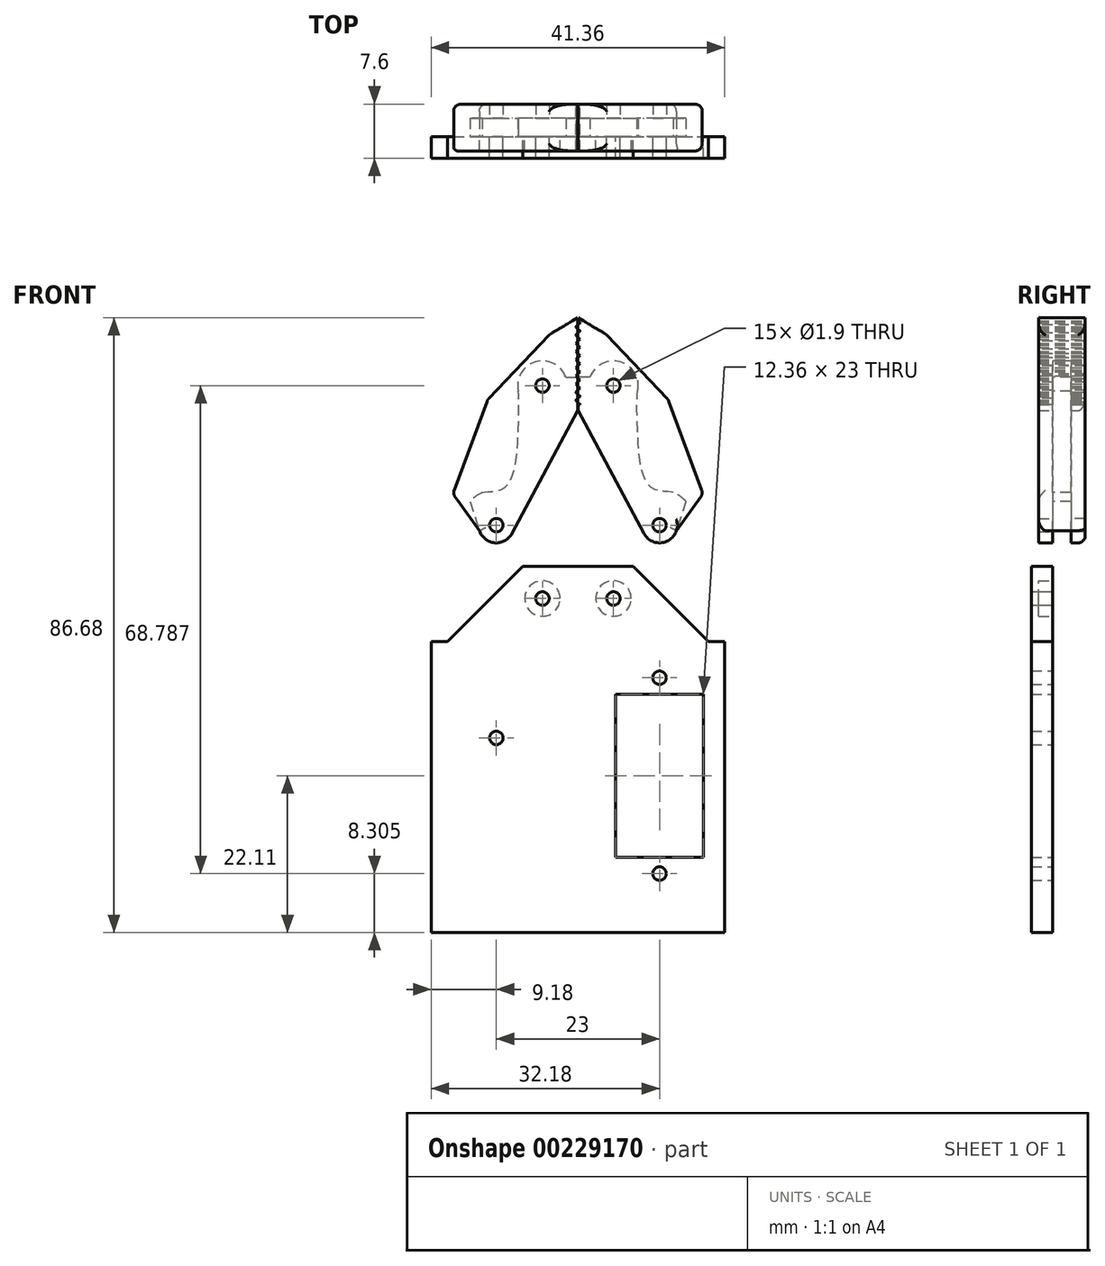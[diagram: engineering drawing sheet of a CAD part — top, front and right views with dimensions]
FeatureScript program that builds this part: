
annotation { "Feature Type Name" : "Feature", "Feature Type Description" : "" }
export const myFeature = defineFeature(function(context is Context, id is Id, definition is map)
    precondition{}
    {
        {
            var Q0;
            Q0=qCreatedBy(makeId("Front.planeOp"),FACE);
            var sketch = newSketch(context, id + "F0", { "sketchPlane" : qUnion([Q0])});
            skLineSegment(sketch, "E0.top", {"start": v(17.68, -22.43) * mm, "end": v(5.32, -22.43) * mm});
            skLineSegment(sketch, "E0.left", {"start": v(18.36, 12.56) * mm, "end": v(18.36, -22.43) * mm});
            skLineSegment(sketch, "E0.right", {"start": v(-18.36, 12.56) * mm, "end": v(-18.36, -22.43) * mm});
            skPoint(sketch, "E0.middle", {"position": v(0, 0) * mm});
            skLineSegment(sketch, "E1.bottom", {"start": v(5.32, -22.43) * mm, "end": v(17.68, -22.43) * mm});
            skLineSegment(sketch, "E1.top", {"start": v(5.32, 5.18) * mm, "end": v(17.68, 5.18) * mm});
            skLineSegment(sketch, "E1.left", {"start": v(5.32, -22.43) * mm, "end": v(5.32, 5.18) * mm});
            skLineSegment(sketch, "E1.right", {"start": v(17.68, -22.43) * mm, "end": v(17.68, 5.18) * mm});
            skLineSegment(sketch, "E2.bottom", {"start": v(5.32, 0) * mm, "end": v(17.68, 0) * mm});
            skLineSegment(sketch, "E2.top", {"start": v(5.32, -17.82) * mm, "end": v(17.68, -17.82) * mm});
            skLineSegment(sketch, "E2.left", {"start": v(5.32, 0) * mm, "end": v(5.32, -17.82) * mm});
            skLineSegment(sketch, "E2.right", {"start": v(17.68, 0) * mm, "end": v(17.68, -17.82) * mm});
            skLineSegment(sketch, "E3.bottom", {"start": v(17.68, 5.18) * mm, "end": v(5.32, 5.18) * mm});
            skLineSegment(sketch, "E3.top", {"start": v(17.68, 9.8) * mm, "end": v(5.32, 9.8) * mm});
            skLineSegment(sketch, "E3.left", {"start": v(17.68, 5.18) * mm, "end": v(17.68, 9.8) * mm});
            skLineSegment(sketch, "E3.right", {"start": v(5.32, 5.18) * mm, "end": v(5.32, 9.8) * mm});
            skLineSegment(sketch, "E4", {"start": v(5.32, 9.8) * mm, "end": v(17.68, 5.18) * mm, "construction": true});
            skLineSegment(sketch, "E5", {"start": v(5.32, -17.82) * mm, "end": v(17.68, -22.43) * mm, "construction": true});
            skCircle(sketch, "E6", {"center": v(11.5, 7.49) * mm, "radius": 0.95 * mm});
            skLineSegment(sketch, "E7.top", {"start": v(-18.36, -25.43) * mm, "end": v(18.36, -25.43) * mm});
            skLineSegment(sketch, "E7.left", {"start": v(-18.36, -22.43) * mm, "end": v(-18.36, -25.43) * mm});
            skLineSegment(sketch, "E7.right", {"start": v(18.36, -22.43) * mm, "end": v(18.36, -25.43) * mm});
            skLineSegment(sketch, "E8", {"start": v(0, 32.14) * mm, "end": v(0, 0) * mm, "construction": true});
            skLineSegment(sketch, "E9", {"start": v(-18.36, 0) * mm, "end": v(18.36, 0) * mm, "construction": true});
            skCircle(sketch, "E10", {"center": v(11.5, -20.12) * mm, "radius": 0.95 * mm});
            skLineSegment(sketch, "E11.top", {"start": v(-18.36, -28.43) * mm, "end": v(18.36, -28.43) * mm});
            skLineSegment(sketch, "E11.left", {"start": v(-18.36, -25.43) * mm, "end": v(-18.36, -28.43) * mm});
            skLineSegment(sketch, "E11.right", {"start": v(18.36, -25.43) * mm, "end": v(18.36, -28.43) * mm});
            skLineSegment(sketch, "E12", {"start": v(-18.36, 12.56) * mm, "end": v(-7.75, 23.16) * mm});
            skLineSegment(sketch, "E13", {"start": v(7.75, 23.16) * mm, "end": v(18.36, 12.56) * mm});
            skLineSegment(sketch, "E14", {"start": v(-18.36, 12.56) * mm, "end": v(-18.36, 23.16) * mm, "construction": true});
            skLineSegment(sketch, "E15", {"start": v(18.36, 12.56) * mm, "end": v(18.36, 23.49) * mm, "construction": true});
            skCircle(sketch, "E16", {"center": v(-5, 18.66) * mm, "radius": 0.95 * mm});
            skCircle(sketch, "E17", {"center": v(5, 18.66) * mm, "radius": 0.95 * mm});
            skCircle(sketch, "E18", {"center": v(-11.5, -1) * mm, "radius": 0.95 * mm});
            skLineSegment(sketch, "E19", {"start": v(-7.75, 23.16) * mm, "end": v(7.75, 23.16) * mm});
            skCircle(sketch, "E20", {"center": v(11.5, -1) * mm, "radius": 6.18 * mm});
            skLineSegment(sketch, "E21", {"start": v(11.5, -1) * mm, "end": v(-6.79, -1) * mm, "construction": true});
            skLineSegment(sketch, "E22", {"start": v(-10.25, -1) * mm, "end": v(-10.25, 21.43) * mm, "construction": true});
            skLineSegment(sketch, "E23", {"start": v(18.36, 12.56) * mm, "end": v(20.68, 12.56) * mm});
            skLineSegment(sketch, "E24", {"start": v(20.68, 12.56) * mm, "end": v(20.68, -28.43) * mm});
            skLineSegment(sketch, "E25", {"start": v(-18.36, 12.56) * mm, "end": v(-20.68, 12.56) * mm});
            skLineSegment(sketch, "E26", {"start": v(-20.68, 12.56) * mm, "end": v(-20.68, -28.43) * mm});
            skLineSegment(sketch, "E27", {"start": v(-20.68, -28.43) * mm, "end": v(-18.36, -28.43) * mm});
            skLineSegment(sketch, "E28", {"start": v(18.36, -25.43) * mm, "end": v(20.68, -25.43) * mm});
            skLineSegment(sketch, "E29", {"start": v(20.68, -25.43) * mm, "end": v(-20.68, -25.43) * mm});
            skLineSegment(sketch, "E30", {"start": v(20.68, -28.43) * mm, "end": v(18.36, -28.43) * mm});
            skSolve(sketch);
        }
        {
            var Q0;
            {var subQ1=makeQuery(id+"F0.imprint","IMPRINT",EDGE,{"derivedFrom":sQuery(id+"F0.wireOp",EDGE,"E7.top")});var subQ9=makeQuery(id+"F0.imprint","IMPRINT",EDGE,{"derivedFrom":sQuery(id+"F0.wireOp",EDGE,"E0.right")});var subQ10=makeQuery(id+"F0.imprint","IMPRINT",EDGE,{"derivedFrom":sQuery(id+"F0.wireOp",EDGE,"E0.left")});var subQ16=sQuery(id+"F0.wireOp",EDGE,"E0.top");var subQ20=makeQuery(id+"F0.imprint","IMPRINT",EDGE,{"derivedFrom":sQuery(id+"F0.wireOp",EDGE,"E11.left")});var subQ21=makeQuery(id+"F0.imprint","IMPRINT",EDGE,{"derivedFrom":sQuery(id+"F0.wireOp",EDGE,"E11.right")});Q0=qUnion([makeQuery(id+"F0.imprint","IMPRINT",FACE,{"disambiguationData":[TD([[subQ10,1.0]])]}),makeQuery(id+"F0.imprint","IMPRINT",FACE,{"disambiguationData":[TD([[subQ9,-1.0]])]}),makeQuery(id+"F0.imprint","IMPRINT",FACE,{"disambiguationData":[TD([[subQ20,-1.0]])]}),makeQuery(id+"F0.imprint","IMPRINT",FACE,{"disambiguationData":[TD([[subQ21,1.0]])]}),makeQuery(id+"F0.imprint","IMPRINT",FACE,{"disambiguationData":[TD([[subQ1,-1.0]])]}),makeQuery(id+"F0.imprint","IMPRINT",FACE,{"disambiguationData":[TD([[makeQuery(id+"F0.imprint","IMPRINT",EDGE,{"derivedFrom":subQ16}),1.0]])]})]);}
            var Q1;
            {var subQ2=sQuery(id+"F0.wireOp",EDGE,"E0.top");Q1=makeQuery(id+"F0.imprint","IMPRINT",FACE,{"disambiguationData":[TD([[makeQuery(id+"F0.imprint","IMPRINT",EDGE,{"derivedFrom":subQ2}),-1.0]])]});}
            var Q2;
            Q2=makeQuery(id+"F0.imprint","IMPRINT",FACE,{"disambiguationData":[TD([[makeQuery(id+"F0.imprint","IMPRINT",EDGE,{"derivedFrom":sQuery(id+"F0.wireOp",EDGE,"E3.top")}),1.0]])]});
            var Q3;
            {var subQ0=sQuery(id+"F0.wireOp",EDGE,"E3.bottom");var subQ1=sQuery(id+"F0.wireOp",EDGE,"FkeFUImi-7huS-bPcJ-8ver-gJrOx2cKMFpE");var subQ2=makeQuery(id+"F0.imprint","INTERSECT",VERTEX,{"disambiguationData":[OD(0.0)],"derivedFrom":[subQ1,subQ0]});Q3=makeQuery(id+"F0.imprint","IMPRINT",FACE,{"disambiguationData":[TD([[makeQuery(id+"F0.imprint","IMPRINT",EDGE,{"disambiguationData":[TD([[subQ2,-1.0]])],"derivedFrom":subQ1}),1.0]])]});}
            extrude(context, id + "F1", {"entities" : qUnion([Q0, Q1, Q2, Q3]), "depth" : 3 * mm});
        }
        {
            var Q0;
            Q0=makeQuery(id+"F0.imprint","IMPRINT",FACE,{"disambiguationData":[TD([[makeQuery(id+"F0.imprint","IMPRINT",EDGE,{"derivedFrom":sQuery(id+"F0.wireOp",EDGE,"E0.left")}),-1.0]])]});
            var sketch = newSketch(context, id + "F2", { "sketchPlane" : qUnion([Q0])});
            skCircle(sketch, "E31", {"center": v(-5, 18.66) * mm, "radius": 0.95 * mm});
            skCircle(sketch, "E32", {"center": v(5, 18.66) * mm, "radius": 0.95 * mm});
            skCircle(sketch, "E33", {"center": v(5, 18.66) * mm, "radius": 2.5 * mm});
            skCircle(sketch, "E34", {"center": v(-5, 18.66) * mm, "radius": 2.5 * mm});
            skCircle(sketch, "E35", {"center": v(-5, 48.66) * mm, "radius": 2.5 * mm});
            skLineSegment(sketch, "E36", {"start": v(-5, 18.66) * mm, "end": v(-5, 48.66) * mm});
            skLineSegment(sketch, "E37", {"start": v(-11.5, -1) * mm, "end": v(-11.5, 29) * mm});
            skCircle(sketch, "E38", {"center": v(-11.5, 29) * mm, "radius": 2.5 * mm});
            skCircle(sketch, "E39", {"center": v(-5, 48.66) * mm, "radius": 0.95 * mm});
            skCircle(sketch, "E40", {"center": v(-11.5, 29) * mm, "radius": 0.95 * mm});
            skLineSegment(sketch, "E41", {"start": v(0, 85.35) * mm, "end": v(-3, 85.35) * mm});
            skLineSegment(sketch, "E42", {"start": v(-21.12, 18.52) * mm, "end": v(-21.12, 50.54) * mm, "construction": true});
            skLineSegment(sketch, "E43.direction1", {"start": v(0, 82.52) * mm, "end": v(25, 82.52) * mm, "construction": true});
            skLineSegment(sketch, "E43.direction2", {"start": v(0, 82.52) * mm, "end": v(0, 82.52) * mm, "construction": true});
            skLineSegment(sketch, "E44.trimOffspring", {"start": v(-0.3, 51.2) * mm, "end": v(-0.3, 51.2) * mm});
            skLineSegment(sketch, "E45.trimOffspring", {"start": v(0, 82.52) * mm, "end": v(0, 82.52) * mm});
            skLineSegment(sketch, "E46", {"start": v(0, 45.16) * mm, "end": v(-9.3, 27.82) * mm});
            skLineSegment(sketch, "E47", {"start": v(-15.21, 32.35) * mm, "end": v(-13.88, 28.23) * mm});
            skArc(sketch, "E48", {"start": v(-13.46, 33.6) * mm, "mid": v(-14.4, 33.07) * mm, "end": v(-15.21, 32.35) * mm});
            skLineSegment(sketch, "E49", {"start": v(0, 85.35) * mm, "end": v(0, 73.2) * mm});
            skLineSegment(sketch, "E50.trimOffspring", {"start": v(0, 54.96) * mm, "end": v(0, 45.16) * mm});
            skPoint(sketch, "E51.visualSharp", {"position": v(-12.13, 33.96) * mm});
            skLineSegment(sketch, "E52", {"start": v(0, 54.96) * mm, "end": v(0, 73.2) * mm});
            skLineSegment(sketch, "E53", {"start": v(-3.95, 55.9) * mm, "end": v(0, 58.26) * mm});
            skLineSegment(sketch, "E54", {"start": v(0, 58.26) * mm, "end": v(-3.95, 55.9) * mm});
            skLineSegment(sketch, "E55", {"start": v(-2.5, 48.79) * mm, "end": v(-2.5, 18.66) * mm, "construction": true});
            skLineSegment(sketch, "E56", {"start": v(-7.5, 48.66) * mm, "end": v(-7.5, 18.66) * mm, "construction": true});
            skFitSpline(sketch, "E57", {"points": [v(-13.46, 33.6) * mm, v(-10.5, 34.2) * mm, v(-8.48, 40.92) * mm, v(-8.42, 47.9) * mm], "startDerivative": vector(5.15, 2.53) * mm, "endDerivative": vector(-1.23, 9.61) * mm});
            skCircle(sketch, "E58", {"center": v(-5, 48.66) * mm, "radius": 3.5 * mm});
            skLineSegment(sketch, "E59", {"start": v(-3.95, 55.9) * mm, "end": v(-6.13, 53.44) * mm});
            skLineSegment(sketch, "E60", {"start": v(-12.74, 46.65) * mm, "end": v(-17.64, 33.43) * mm});
            skLineSegment(sketch, "E61", {"start": v(-17.64, 33.43) * mm, "end": v(-13.88, 28.23) * mm});
            skLineSegment(sketch, "E62", {"start": v(-3.95, 55.9) * mm, "end": v(-12.74, 46.65) * mm});
            skLineSegment(sketch, "E63", {"start": v(-12.74, 46.65) * mm, "end": v(-12.74, 46.65) * mm});
            skLineSegment(sketch, "E64", {"start": v(0, 45.16) * mm, "end": v(-1.71, 49.86) * mm});
            skPoint(sketch, "E65.orphan", {"position": v(-2.2, 51.2) * mm});
            skLineSegment(sketch, "E66", {"start": v(-1.71, 49.86) * mm, "end": v(0, 49.86) * mm});
            skSolve(sketch);
        }
        {
            var Q0;
            Q0=qSketchRegion(id+"F2",true);
            var Q1;
            Q1=makeQuery(id+"F2.imprint","IMPRINT",FACE,{"disambiguationData":[TD([[makeQuery(id+"F2.imprint","IMPRINT",EDGE,{"derivedFrom":sQuery(id+"F2.wireOp",EDGE,"E35")}),-1.0]])]});
            var Q2;
            Q2=makeQuery(id+"F2.imprint","IMPRINT",FACE,{"disambiguationData":[TD([[makeQuery(id+"F2.imprint","IMPRINT",EDGE,{"derivedFrom":sQuery(id+"F2.wireOp",EDGE,"E35")}),1.0]])]});
            extrude(context, id + "F3", {"entities" : qUnion([Q0, Q1, Q2]), "depth" : 2 * mm, "offsetDistance" : 25 * mm});
        }
        {
            var Q0;
            Q0=makeQuery(id+"F3.opExtrude","CAP_FACE",FACE,{"disambiguationData":[OSD([sQuery(id+"F2.wireOp",EDGE,"E38"),sQuery(id+"F2.wireOp",EDGE,"E39"),sQuery(id+"F2.wireOp",EDGE,"E40"),sQuery(id+"F2.wireOp",EDGE,"ojlclZL8-mFRy-oj94-TuiW-mkqWwnsQ5PH2"),sQuery(id+"F2.wireOp",EDGE,"E41"),sQuery(id+"F2.wireOp",EDGE,"3BnPoFJo-80Xj-sxFC-LyH3-L9wn1PanijBF"),sQuery(id+"F2.wireOp",EDGE,"nw0cncdo-VvPd-ihfL-C2Mb-7qvmsGwaHwNe"),sQuery(id+"F2.wireOp",EDGE,"uXCrYnIw-o2L2-LL2c-z51U-zKsu6KjcqbaR"),sQuery(id+"F2.wireOp",EDGE,"VJ0x262G-N5hV-EgR8-y2wY-FNzAg9Ctw9Hw"),sQuery(id+"F2.wireOp",EDGE,"E1BABdde-z93K-BAIA-5H2X-Xf3NOflcem9W"),sQuery(id+"F2.wireOp",EDGE,"d5e632d6-f1cd-457d-8b80-b158a3dd6426.filletArc"),sQuery(id+"F2.wireOp",EDGE,"XKeZV852-5iyM-pWoH-Hqqh-tp7GCyPhfXws"),sQuery(id+"F2.wireOp",EDGE,"KprPelza-mhI2-seXi-sNop-6tTakIu092JH"),sQuery(id+"F2.wireOp",EDGE,"tiWxGrWV-pEby-lTsz-UDt3-zo9YDZITsxui"),sQuery(id+"F2.wireOp",EDGE,"c9GPy7wp-Q1am-ekVC-Z5kS-GpAEriY1IEmJ"),sQuery(id+"F2.wireOp",EDGE,"E43.0.1.0"),sQuery(id+"F2.wireOp",EDGE,"E43.0.1.1"),sQuery(id+"F2.wireOp",EDGE,"E43.0.1.2"),sQuery(id+"F2.wireOp",EDGE,"E43.0.1.3"),sQuery(id+"F2.wireOp",EDGE,"E43.0.2.0"),sQuery(id+"F2.wireOp",EDGE,"E43.0.2.1"),sQuery(id+"F2.wireOp",EDGE,"E43.0.2.2"),sQuery(id+"F2.wireOp",EDGE,"E43.0.2.3"),sQuery(id+"F2.wireOp",EDGE,"E43.0.3.0"),sQuery(id+"F2.wireOp",EDGE,"E43.0.3.1"),sQuery(id+"F2.wireOp",EDGE,"E43.0.10.2"),sQuery(id+"F2.wireOp",EDGE,"E43.0.10.3"),sQuery(id+"F2.wireOp",EDGE,"E43.0.11.0"),sQuery(id+"F2.wireOp",EDGE,"E43.0.11.1"),sQuery(id+"F2.wireOp",EDGE,"E43.0.11.2"),sQuery(id+"F2.wireOp",EDGE,"E43.0.11.3"),sQuery(id+"F2.wireOp",EDGE,"E43.0.12.0"),sQuery(id+"F2.wireOp",EDGE,"E43.0.12.1"),sQuery(id+"F2.wireOp",EDGE,"E43.0.12.2"),sQuery(id+"F2.wireOp",EDGE,"E43.0.12.3"),sQuery(id+"F2.wireOp",EDGE,"E43.0.13.0"),sQuery(id+"F2.wireOp",EDGE,"E43.0.13.1"),sQuery(id+"F2.wireOp",EDGE,"8374c501-d780-4c48-9e4f-f82781ded212.trimOffspring")])],"isStart":true});
            cPlane(context, id + "F4", {"entities" : qUnion([Q0]), "cplaneType" : CPlaneType.OFFSET, "offset" : 1.3 * mm, "width" : 150 * mm, "height" : 150 * mm});
        }
        {
            var Q0;
            Q0=makeQuery(id+"F3.opExtrude","SWEPT_BODY",BODY,{"disambiguationData":[OSD([sQuery(id+"F2.wireOp",EDGE,"3G5pYEca-LQFK-HRrX-UVoz-krPxFwjwMmPq"),sQuery(id+"F2.wireOp",EDGE,"D40M5MyK-hRGI-8Rlu-RpBH-azIpfS1hm2Ch"),sQuery(id+"F2.wireOp",EDGE,"s1k57Acv-ITZD-CSzE-UE93-I8YxeqDDyJKU"),sQuery(id+"F2.wireOp",EDGE,"5y2t2k9P-78OV-HH9a-51na-ZKo10bDWfkAO"),sQuery(id+"F2.wireOp",EDGE,"Qi3x5NGB-qysZ-amDF-UYud-FMr6MCnc7aq0"),sQuery(id+"F2.wireOp",EDGE,"cTroWyKG-EG0o-9xHU-UcJ6-KtfM8Qy8pXZp"),sQuery(id+"F2.wireOp",EDGE,"e1913aee-df30-4620-9d8e-7543e42c2ca5.0.1.0"),sQuery(id+"F2.wireOp",EDGE,"e1913aee-df30-4620-9d8e-7543e42c2ca5.0.1.1"),sQuery(id+"F2.wireOp",EDGE,"e1913aee-df30-4620-9d8e-7543e42c2ca5.0.1.2"),sQuery(id+"F2.wireOp",EDGE,"e1913aee-df30-4620-9d8e-7543e42c2ca5.0.1.3"),sQuery(id+"F2.wireOp",EDGE,"e1913aee-df30-4620-9d8e-7543e42c2ca5.0.2.0"),sQuery(id+"F2.wireOp",EDGE,"e1913aee-df30-4620-9d8e-7543e42c2ca5.0.2.1"),sQuery(id+"F2.wireOp",EDGE,"e1913aee-df30-4620-9d8e-7543e42c2ca5.0.2.2"),sQuery(id+"F2.wireOp",EDGE,"e1913aee-df30-4620-9d8e-7543e42c2ca5.0.2.3"),sQuery(id+"F2.wireOp",EDGE,"e1913aee-df30-4620-9d8e-7543e42c2ca5.0.3.0"),sQuery(id+"F2.wireOp",EDGE,"e1913aee-df30-4620-9d8e-7543e42c2ca5.0.3.1"),sQuery(id+"F2.wireOp",EDGE,"e1913aee-df30-4620-9d8e-7543e42c2ca5.0.3.2"),sQuery(id+"F2.wireOp",EDGE,"e1913aee-df30-4620-9d8e-7543e42c2ca5.0.3.3"),sQuery(id+"F2.wireOp",EDGE,"e1913aee-df30-4620-9d8e-7543e42c2ca5.0.9.0"),sQuery(id+"F2.wireOp",EDGE,"e1913aee-df30-4620-9d8e-7543e42c2ca5.0.9.1"),sQuery(id+"F2.wireOp",EDGE,"e1913aee-df30-4620-9d8e-7543e42c2ca5.0.9.2"),sQuery(id+"F2.wireOp",EDGE,"e1913aee-df30-4620-9d8e-7543e42c2ca5.0.9.3"),sQuery(id+"F2.wireOp",EDGE,"20ddf6a0-ac28-4d51-8821-c515d868528c.trimOffspring"),sQuery(id+"F2.wireOp",EDGE,"bb4553dc-da2a-40c6-8fb4-93eda76ad95e.trimOffspring"),sQuery(id+"F2.wireOp",EDGE,"H0zLOWRU-mUu9-J1aP-kU96-gJEbAY07lwdY"),sQuery(id+"F2.wireOp",EDGE,"IEDIgM9O-5oWb-OJ2w-YNWq-edb6KWvRt9Rm"),sQuery(id+"F2.wireOp",EDGE,"apXkyRii-zMPp-zWOI-7xWW-YDyuhudw0k6Z"),sQuery(id+"F2.wireOp",EDGE,"E38"),sQuery(id+"F2.wireOp",EDGE,"HaXWiWXE-dKqc-4Mvg-dvKj-iTskoXOZy6q7"),sQuery(id+"F2.wireOp",EDGE,"h57rnF5O-WBu1-dYab-qGXE-qs2SRwkzpOeQ"),sQuery(id+"F2.wireOp",EDGE,"p5iCMnno-PPcU-yOzt-AC88-Hf3pu4jtTxLl"),sQuery(id+"F2.wireOp",EDGE,"ae112758-d8a4-4d5f-8063-ec1446f6f22f.filletArc"),sQuery(id+"F2.wireOp",EDGE,"E39"),sQuery(id+"F2.wireOp",EDGE,"E40")])]});
            var Q1;
            Q1=qCreatedBy(id+"F4.planeOp",FACE);
            mirror(context, id + "F5", {"entities" : qUnion([Q0]), "mirrorPlane" : qUnion([Q1])});
        }
        {
            var Q0;
            Q0=makeQuery(id+"F2.imprint","IMPRINT",FACE,{"disambiguationData":[TD([[makeQuery(id+"F2.imprint","IMPRINT",EDGE,{"derivedFrom":sQuery(id+"F2.wireOp",EDGE,"E47")}),-1.0]])]});
            extrude(context, id + "F6", {"entities" : qUnion([Q0]), "operationType" : NewBodyOperationType.ADD, "oppositeDirection" : true, "depth" : 2.6 * mm, "offsetDistance" : 25 * mm});
        }
        {
            var Q0;
            Q0=makeQuery(id+"F3.opExtrude","SWEPT_BODY",BODY,{"disambiguationData":[OSD([sQuery(id+"F2.wireOp",EDGE,"E38"),sQuery(id+"F2.wireOp",EDGE,"E39"),sQuery(id+"F2.wireOp",EDGE,"E40"),sQuery(id+"F2.wireOp",EDGE,"E46"),sQuery(id+"F2.wireOp",EDGE,"E50.trimOffspring"),sQuery(id+"F2.wireOp",EDGE,"E52"),sQuery(id+"F2.wireOp",EDGE,"E54"),sQuery(id+"F2.wireOp",EDGE,"E60"),sQuery(id+"F2.wireOp",EDGE,"E61"),sQuery(id+"F2.wireOp",EDGE,"E62")])]});
            var Q1;
            Q1=qCreatedBy(makeId("Right.planeOp"),FACE);
            mirror(context, id + "F7", {"operationType" : NewBodyOperationType.ADD, "entities" : qUnion([Q0]), "mirrorPlane" : qUnion([Q1])});
        }
        {
            var Q0;
            {var subQ0=makeQuery(id+"F5.opPattern","COPY",FACE,{"derivedFrom":makeQuery(id+"F3.opExtrude","CAP_FACE",FACE,{"disambiguationData":[OSD([sQuery(id+"F2.wireOp",EDGE,"E38"),sQuery(id+"F2.wireOp",EDGE,"E39"),sQuery(id+"F2.wireOp",EDGE,"E40"),sQuery(id+"F2.wireOp",EDGE,"E46"),sQuery(id+"F2.wireOp",EDGE,"E50.trimOffspring"),sQuery(id+"F2.wireOp",EDGE,"E52"),sQuery(id+"F2.wireOp",EDGE,"E54"),sQuery(id+"F2.wireOp",EDGE,"E60"),sQuery(id+"F2.wireOp",EDGE,"E61"),sQuery(id+"F2.wireOp",EDGE,"E62")])],"isStart":false}),"instanceName":"1"});Q0=makeQuery(id+"Fyi3DaJtYUeMCXP_7.splitOp","SPLIT",FACE,{"derivedFrom":makeQuery(id+"F7.boolean.opBoolean","MERGE",FACE,{"derivedFrom":[subQ0,makeQuery(id+"F7.opPattern","COPY",FACE,{"derivedFrom":subQ0,"instanceName":"1"})]})});}
            var sketch = newSketch(context, id + "F8", { "sketchPlane" : qUnion([Q0])});
            skLineSegment(sketch, "E67.left", {"start": v(-0.28, 57.52) * mm, "end": v(-0.28, 57.5) * mm});
            skLineSegment(sketch, "E67.right", {"start": v(0.29, 58.09) * mm, "end": v(0.29, 58.08) * mm});
            skLineSegment(sketch, "E68.direction1", {"start": v(0.29, 56.94) * mm, "end": v(25.29, 56.94) * mm, "construction": true});
            skLineSegment(sketch, "E68.direction2", {"start": v(0.29, 56.94) * mm, "end": v(0.29, 56.93) * mm, "construction": true});
            skLineSegment(sketch, "E69", {"start": v(0, 57.8) * mm, "end": v(-0.28, 57.52) * mm});
            skLineSegment(sketch, "E70", {"start": v(0, 57.8) * mm, "end": v(-0.28, 57.51) * mm});
            skPoint(sketch, "E71.orphan", {"position": v(-0.3, 57.51) * mm});
            skLineSegment(sketch, "E72", {"start": v(-0.28, 57.51) * mm, "end": v(0.29, 56.95) * mm});
            skLineSegment(sketch, "E73", {"start": v(-0.28, 57.5) * mm, "end": v(0.29, 56.93) * mm});
            skLineSegment(sketch, "E74.0.1.0", {"start": v(0.28, 56.93) * mm, "end": v(-0.28, 56.37) * mm});
            skLineSegment(sketch, "E74.0.1.1", {"start": v(0.29, 56.93) * mm, "end": v(-0.28, 56.36) * mm});
            skLineSegment(sketch, "E74.0.1.2", {"start": v(-0.28, 56.36) * mm, "end": v(0.29, 55.8) * mm});
            skLineSegment(sketch, "E74.0.1.3", {"start": v(-0.28, 56.36) * mm, "end": v(0.29, 55.78) * mm});
            skLineSegment(sketch, "E74.0.2.0", {"start": v(0.28, 55.78) * mm, "end": v(-0.28, 55.22) * mm});
            skLineSegment(sketch, "E74.0.2.1", {"start": v(0.29, 55.78) * mm, "end": v(-0.28, 55.2) * mm});
            skLineSegment(sketch, "E74.0.2.2", {"start": v(-0.28, 55.21) * mm, "end": v(0.29, 54.65) * mm});
            skLineSegment(sketch, "E74.0.2.3", {"start": v(-0.28, 55.2) * mm, "end": v(0.29, 54.63) * mm});
            skLineSegment(sketch, "E74.0.3.0", {"start": v(0.28, 54.63) * mm, "end": v(-0.28, 54.07) * mm});
            skLineSegment(sketch, "E74.0.3.1", {"start": v(0.29, 54.63) * mm, "end": v(-0.28, 54.06) * mm});
            skLineSegment(sketch, "E74.0.3.2", {"start": v(-0.28, 54.06) * mm, "end": v(0.29, 53.5) * mm});
            skLineSegment(sketch, "E74.0.3.3", {"start": v(-0.28, 54.06) * mm, "end": v(0.29, 53.48) * mm});
            skLineSegment(sketch, "E74.0.4.0", {"start": v(0.28, 53.48) * mm, "end": v(-0.28, 52.92) * mm});
            skLineSegment(sketch, "E74.0.4.1", {"start": v(0.29, 53.48) * mm, "end": v(-0.28, 52.9) * mm});
            skLineSegment(sketch, "E74.0.4.2", {"start": v(-0.28, 52.91) * mm, "end": v(0.29, 52.35) * mm});
            skLineSegment(sketch, "E74.0.4.3", {"start": v(-0.28, 52.9) * mm, "end": v(0.29, 52.33) * mm});
            skLineSegment(sketch, "E74.0.5.0", {"start": v(0.28, 52.33) * mm, "end": v(-0.28, 51.77) * mm});
            skLineSegment(sketch, "E74.0.5.1", {"start": v(0.29, 52.33) * mm, "end": v(-0.28, 51.76) * mm});
            skLineSegment(sketch, "E74.0.5.2", {"start": v(-0.28, 51.76) * mm, "end": v(0.29, 51.2) * mm});
            skLineSegment(sketch, "E74.0.5.3", {"start": v(-0.28, 51.76) * mm, "end": v(0.28, 51.18) * mm});
            skLineSegment(sketch, "E74.0.6.0", {"start": v(0.28, 51.18) * mm, "end": v(-0.28, 50.62) * mm});
            skLineSegment(sketch, "E74.0.6.1", {"start": v(0.29, 51.18) * mm, "end": v(-0.28, 50.61) * mm});
            skLineSegment(sketch, "E74.0.6.2", {"start": v(-0.28, 50.61) * mm, "end": v(0.29, 50.05) * mm});
            skLineSegment(sketch, "E74.0.6.3", {"start": v(-0.28, 50.6) * mm, "end": v(0.28, 50.03) * mm});
            skLineSegment(sketch, "E74.0.7.0", {"start": v(0.28, 50.03) * mm, "end": v(-0.28, 49.47) * mm});
            skLineSegment(sketch, "E74.0.7.1", {"start": v(0.29, 50.03) * mm, "end": v(-0.28, 49.46) * mm});
            skLineSegment(sketch, "E74.0.7.2", {"start": v(-0.28, 49.46) * mm, "end": v(0.29, 48.9) * mm});
            skLineSegment(sketch, "E74.0.7.3", {"start": v(-0.28, 49.46) * mm, "end": v(0.28, 48.88) * mm});
            skLineSegment(sketch, "E74.0.8.0", {"start": v(0.28, 48.88) * mm, "end": v(-0.28, 48.32) * mm});
            skLineSegment(sketch, "E74.0.8.1", {"start": v(0.29, 48.88) * mm, "end": v(-0.28, 48.31) * mm});
            skLineSegment(sketch, "E74.0.8.2", {"start": v(-0.28, 48.31) * mm, "end": v(0.29, 47.75) * mm});
            skLineSegment(sketch, "E74.0.8.3", {"start": v(-0.28, 48.3) * mm, "end": v(0.28, 47.73) * mm});
            skLineSegment(sketch, "E74.0.9.0", {"start": v(0.28, 47.73) * mm, "end": v(-0.28, 47.17) * mm});
            skLineSegment(sketch, "E74.0.9.1", {"start": v(0.29, 47.73) * mm, "end": v(-0.28, 47.16) * mm});
            skLineSegment(sketch, "E74.0.9.2", {"start": v(-0.28, 47.16) * mm, "end": v(0.29, 46.6) * mm});
            skLineSegment(sketch, "E74.0.9.3", {"start": v(-0.28, 47.16) * mm, "end": v(0.28, 46.58) * mm});
            skLineSegment(sketch, "E74.direction1", {"start": v(-0.28, 57.52) * mm, "end": v(24.71, 57.52) * mm, "construction": true});
            skLineSegment(sketch, "E74.direction2", {"start": v(-0.28, 57.52) * mm, "end": v(-0.28, 57.5) * mm, "construction": true});
            skLineSegment(sketch, "E75", {"start": v(0.28, 46.58) * mm, "end": v(-0.28, 46.03) * mm});
            skLineSegment(sketch, "E76", {"start": v(0.29, 46.58) * mm, "end": v(-0.28, 46.01) * mm});
            skLineSegment(sketch, "E77", {"start": v(-0.28, 46.01) * mm, "end": v(0, 46.01) * mm});
            skLineSegment(sketch, "E78", {"start": v(-0.28, 46.01) * mm, "end": v(-0.28, 46) * mm});
            skLineSegment(sketch, "E79", {"start": v(-0.28, 46) * mm, "end": v(0, 46) * mm});
            skLineSegment(sketch, "E80.bottom", {"start": v(0, 46.01) * mm, "end": v(0, 46.01) * mm});
            skLineSegment(sketch, "E80.top", {"start": v(0, 45.15) * mm, "end": v(0, 45.15) * mm});
            skLineSegment(sketch, "E80.left", {"start": v(0, 46) * mm, "end": v(0, 45.15) * mm});
            skLineSegment(sketch, "E80.right", {"start": v(0, 46.01) * mm, "end": v(0, 45.15) * mm});
            skPoint(sketch, "E81.start.orphan", {"position": v(0.28, 46.58) * mm});
            skLineSegment(sketch, "E82", {"start": v(0.29, 46.6) * mm, "end": v(0.29, 46.58) * mm});
            skPoint(sketch, "E83.start.orphan", {"position": v(-0.28, 57.5) * mm});
            skLineSegment(sketch, "E84.trimOffspring", {"start": v(0.29, 56.95) * mm, "end": v(0.29, 56.93) * mm});
            skLineSegment(sketch, "E85.trimOffspring", {"start": v(0.29, 55.8) * mm, "end": v(0.29, 55.79) * mm, "construction": true});
            skLineSegment(sketch, "E86.trimOffspring", {"start": v(-0.28, 55.22) * mm, "end": v(-0.28, 55.2) * mm});
            skLineSegment(sketch, "E87.trimOffspring", {"start": v(-0.28, 56.37) * mm, "end": v(-0.28, 56.36) * mm});
            skLineSegment(sketch, "E88.trimOffspring", {"start": v(0.29, 55.8) * mm, "end": v(0.29, 55.78) * mm});
            skLineSegment(sketch, "E89.trimOffspring", {"start": v(0.29, 54.65) * mm, "end": v(0.29, 54.63) * mm});
            skLineSegment(sketch, "E90.trimOffspring", {"start": v(0.29, 53.5) * mm, "end": v(0.29, 53.48) * mm});
            skLineSegment(sketch, "E91.trimOffspring", {"start": v(-0.28, 54.07) * mm, "end": v(-0.28, 54.06) * mm});
            skLineSegment(sketch, "E92.trimOffspring", {"start": v(-0.28, 52.92) * mm, "end": v(-0.28, 52.9) * mm});
            skLineSegment(sketch, "E93.trimOffspring", {"start": v(0.29, 52.35) * mm, "end": v(0.29, 52.33) * mm});
            skLineSegment(sketch, "E94.trimOffspring", {"start": v(-0.28, 51.77) * mm, "end": v(-0.28, 51.76) * mm});
            skLineSegment(sketch, "E95.trimOffspring", {"start": v(-0.28, 50.62) * mm, "end": v(-0.28, 50.6) * mm});
            skLineSegment(sketch, "E96.trimOffspring", {"start": v(0.29, 51.2) * mm, "end": v(0.29, 51.18) * mm});
            skLineSegment(sketch, "E97.trimOffspring", {"start": v(0.29, 50.05) * mm, "end": v(0.29, 50.03) * mm});
            skLineSegment(sketch, "E98.trimOffspring", {"start": v(0.29, 48.9) * mm, "end": v(0.29, 48.88) * mm});
            skLineSegment(sketch, "E99.trimOffspring", {"start": v(0.29, 47.75) * mm, "end": v(0.29, 47.73) * mm});
            skLineSegment(sketch, "E100.trimOffspring", {"start": v(-0.28, 49.47) * mm, "end": v(-0.28, 49.46) * mm});
            skLineSegment(sketch, "E101.trimOffspring", {"start": v(-0.28, 48.32) * mm, "end": v(-0.28, 48.3) * mm});
            skLineSegment(sketch, "E102.trimOffspring", {"start": v(-0.28, 47.17) * mm, "end": v(-0.28, 47.16) * mm});
            skLineSegment(sketch, "E103.trimOffspring", {"start": v(-0.28, 46.03) * mm, "end": v(-0.28, 46.01) * mm});
            skPoint(sketch, "E104.orphan", {"position": v(-0.28, 47.16) * mm});
            skPoint(sketch, "E105.orphan", {"position": v(-0.28, 48.3) * mm});
            skPoint(sketch, "E106.orphan", {"position": v(-0.28, 49.46) * mm});
            skPoint(sketch, "E107.orphan", {"position": v(-0.28, 50.6) * mm});
            skLineSegment(sketch, "E108.bottom", {"start": v(0, 58.26) * mm, "end": v(0, 58.26) * mm});
            skLineSegment(sketch, "E108.left", {"start": v(0, 58.26) * mm, "end": v(0, 57.8) * mm});
            skLineSegment(sketch, "E108.right", {"start": v(0, 58.26) * mm, "end": v(0, 57.8) * mm});
            skSolve(sketch);
        }
        {
            var Q0;
            Q0=qSketchRegion(id+"F8",true);
            extrude(context, id + "F9", {"entities" : qUnion([Q0]), "operationType" : NewBodyOperationType.REMOVE, "oppositeDirection" : true, "depth" : 25 * mm, "offsetDistance" : 25 * mm});
        }
        {
            var Q0;
            Q0=makeQuery(id+"F5.opPattern","COPY",EDGE,{"derivedFrom":makeQuery(id+"F3.opExtrude","CAP_EDGE",EDGE,{"disambiguationData":[OSD([sQuery(id+"F2.wireOp",EDGE,"E60")])],"isStart":false}),"instanceName":"1"});
            var Q1;
            Q1=makeQuery(id+"F5.opPattern","COPY",EDGE,{"derivedFrom":makeQuery(id+"F3.opExtrude","CAP_EDGE",EDGE,{"disambiguationData":[OSD([sQuery(id+"F2.wireOp",EDGE,"E62")])],"isStart":false}),"instanceName":"1"});
            var Q2;
            Q2=makeQuery(id+"F5.opPattern","COPY",EDGE,{"derivedFrom":makeQuery(id+"F3.opExtrude","CAP_EDGE",EDGE,{"disambiguationData":[OSD([sQuery(id+"F2.wireOp",EDGE,"E46")])],"isStart":false}),"instanceName":"1"});
            var Q3;
            Q3=makeQuery(id+"F5.opPattern","COPY",EDGE,{"derivedFrom":makeQuery(id+"F3.opExtrude","CAP_EDGE",EDGE,{"disambiguationData":[OSD([sQuery(id+"F2.wireOp",EDGE,"E61")])],"isStart":false}),"instanceName":"1"});
            var Q4;
            Q4=makeQuery(id+"F3.opExtrude","CAP_EDGE",EDGE,{"disambiguationData":[OSD([sQuery(id+"F2.wireOp",EDGE,"E60")])],"isStart":false});
            var Q5;
            Q5=makeQuery(id+"F3.opExtrude","CAP_EDGE",EDGE,{"disambiguationData":[OSD([sQuery(id+"F2.wireOp",EDGE,"E62")])],"isStart":false});
            var Q6;
            Q6=makeQuery(id+"F3.opExtrude","CAP_EDGE",EDGE,{"disambiguationData":[OSD([sQuery(id+"F2.wireOp",EDGE,"E54")])],"isStart":false});
            var Q7;
            Q7=makeQuery(id+"F7.opPattern","COPY",EDGE,{"derivedFrom":makeQuery(id+"F3.opExtrude","CAP_EDGE",EDGE,{"disambiguationData":[OSD([sQuery(id+"F2.wireOp",EDGE,"E54")])],"isStart":false}),"instanceName":"1"});
            var Q8;
            Q8=makeQuery(id+"F7.opPattern","COPY",EDGE,{"derivedFrom":makeQuery(id+"F3.opExtrude","CAP_EDGE",EDGE,{"disambiguationData":[OSD([sQuery(id+"F2.wireOp",EDGE,"E62")])],"isStart":false}),"instanceName":"1"});
            var Q9;
            Q9=makeQuery(id+"F7.opPattern","COPY",EDGE,{"derivedFrom":makeQuery(id+"F3.opExtrude","CAP_EDGE",EDGE,{"disambiguationData":[OSD([sQuery(id+"F2.wireOp",EDGE,"E60")])],"isStart":false}),"instanceName":"1"});
            var Q10;
            Q10=makeQuery(id+"F7.opPattern","COPY",EDGE,{"derivedFrom":makeQuery(id+"F3.opExtrude","CAP_EDGE",EDGE,{"disambiguationData":[OSD([sQuery(id+"F2.wireOp",EDGE,"E61")])],"isStart":false}),"instanceName":"1"});
            var Q11;
            Q11=makeQuery(id+"F7.opPattern","COPY",EDGE,{"derivedFrom":makeQuery(id+"F5.opPattern","COPY",EDGE,{"derivedFrom":makeQuery(id+"F3.opExtrude","CAP_EDGE",EDGE,{"disambiguationData":[OSD([sQuery(id+"F2.wireOp",EDGE,"E61")])],"isStart":false}),"instanceName":"1"}),"instanceName":"1"});
            var Q12;
            Q12=makeQuery(id+"F7.opPattern","COPY",EDGE,{"derivedFrom":makeQuery(id+"F5.opPattern","COPY",EDGE,{"derivedFrom":makeQuery(id+"F3.opExtrude","CAP_EDGE",EDGE,{"disambiguationData":[OSD([sQuery(id+"F2.wireOp",EDGE,"E60")])],"isStart":false}),"instanceName":"1"}),"instanceName":"1"});
            var Q13;
            Q13=makeQuery(id+"F7.opPattern","COPY",EDGE,{"derivedFrom":makeQuery(id+"F5.opPattern","COPY",EDGE,{"derivedFrom":makeQuery(id+"F3.opExtrude","CAP_EDGE",EDGE,{"disambiguationData":[OSD([sQuery(id+"F2.wireOp",EDGE,"E62")])],"isStart":false}),"instanceName":"1"}),"instanceName":"1"});
            var Q14;
            {var subQ0=sQuery(id+"F2.wireOp",EDGE,"E62");var subQ1=sQuery(id+"F2.wireOp",EDGE,"E60");var subQ2=makeQuery(id+"F3.opExtrude","SWEPT_EDGE",EDGE,{"disambiguationData":[OSD([subQ1,subQ0])]});Q14=makeQuery(id+"F7.opPattern","COPY",EDGE,{"derivedFrom":makeQuery(id+"F6.boolean.opBoolean","MERGE",EDGE,{"derivedFrom":[subQ2,makeQuery(id+"F5.opPattern","COPY",EDGE,{"derivedFrom":subQ2,"instanceName":"1"}),makeQuery(id+"F6.opExtrude","SWEPT_EDGE",EDGE,{"disambiguationData":[OSD([subQ1,subQ0])]})]}),"instanceName":"1"});}
            var Q15;
            {var subQ0=sQuery(id+"F2.wireOp",EDGE,"E61");var subQ1=sQuery(id+"F2.wireOp",EDGE,"E60");var subQ2=makeQuery(id+"F3.opExtrude","SWEPT_EDGE",EDGE,{"disambiguationData":[OSD([subQ1,subQ0])]});Q15=makeQuery(id+"F7.opPattern","COPY",EDGE,{"derivedFrom":makeQuery(id+"F6.boolean.opBoolean","MERGE",EDGE,{"derivedFrom":[subQ2,makeQuery(id+"F5.opPattern","COPY",EDGE,{"derivedFrom":subQ2,"instanceName":"1"}),makeQuery(id+"F6.opExtrude","SWEPT_EDGE",EDGE,{"disambiguationData":[OSD([subQ1,subQ0])]})]}),"instanceName":"1"});}
            var Q16;
            {var subQ0=sQuery(id+"F2.wireOp",EDGE,"E62");var subQ1=sQuery(id+"F2.wireOp",EDGE,"E54");var subQ2=makeQuery(id+"F3.opExtrude","SWEPT_EDGE",EDGE,{"disambiguationData":[OSD([subQ1,subQ0])]});Q16=makeQuery(id+"F7.opPattern","COPY",EDGE,{"derivedFrom":makeQuery(id+"F6.boolean.opBoolean","MERGE",EDGE,{"derivedFrom":[subQ2,makeQuery(id+"F5.opPattern","COPY",EDGE,{"derivedFrom":subQ2,"instanceName":"1"}),makeQuery(id+"F6.opExtrude","SWEPT_EDGE",EDGE,{"disambiguationData":[OSD([subQ1,subQ0])]})]}),"instanceName":"1"});}
            var Q17;
            {var subQ0=sQuery(id+"F2.wireOp",EDGE,"E62");var subQ1=sQuery(id+"F2.wireOp",EDGE,"E54");var subQ2=makeQuery(id+"F3.opExtrude","SWEPT_EDGE",EDGE,{"disambiguationData":[OSD([subQ1,subQ0])]});Q17=makeQuery(id+"F6.boolean.opBoolean","MERGE",EDGE,{"derivedFrom":[subQ2,makeQuery(id+"F5.opPattern","COPY",EDGE,{"derivedFrom":subQ2,"instanceName":"1"}),makeQuery(id+"F6.opExtrude","SWEPT_EDGE",EDGE,{"disambiguationData":[OSD([subQ1,subQ0])]})]});}
            var Q18;
            {var subQ0=sQuery(id+"F2.wireOp",EDGE,"E62");var subQ1=sQuery(id+"F2.wireOp",EDGE,"E60");var subQ2=makeQuery(id+"F3.opExtrude","SWEPT_EDGE",EDGE,{"disambiguationData":[OSD([subQ1,subQ0])]});Q18=makeQuery(id+"F6.boolean.opBoolean","MERGE",EDGE,{"derivedFrom":[subQ2,makeQuery(id+"F5.opPattern","COPY",EDGE,{"derivedFrom":subQ2,"instanceName":"1"}),makeQuery(id+"F6.opExtrude","SWEPT_EDGE",EDGE,{"disambiguationData":[OSD([subQ1,subQ0])]})]});}
            var Q19;
            {var subQ0=sQuery(id+"F2.wireOp",EDGE,"E60");var subQ1=makeQuery(id+"F3.opExtrude","SWEPT_FACE",FACE,{"disambiguationData":[OSD([subQ0])]});Q19=makeQuery(id+"F6.boolean.opBoolean","MERGE",FACE,{"derivedFrom":[subQ1,makeQuery(id+"F5.opPattern","COPY",FACE,{"derivedFrom":subQ1,"instanceName":"1"}),makeQuery(id+"F6.opExtrude","SWEPT_FACE",FACE,{"disambiguationData":[OSD([subQ0])]})]});}
            var Q20;
            Q20=makeQuery(id+"F5.opPattern","COPY",EDGE,{"derivedFrom":makeQuery(id+"F3.opExtrude","CAP_EDGE",EDGE,{"disambiguationData":[OSD([sQuery(id+"F2.wireOp",EDGE,"E54")])],"isStart":false}),"instanceName":"1"});
            var Q21;
            Q21=makeQuery(id+"F7.opPattern","COPY",EDGE,{"derivedFrom":makeQuery(id+"F5.opPattern","COPY",EDGE,{"derivedFrom":makeQuery(id+"F3.opExtrude","CAP_EDGE",EDGE,{"disambiguationData":[OSD([sQuery(id+"F2.wireOp",EDGE,"E54")])],"isStart":false}),"instanceName":"1"}),"instanceName":"1"});
            var Q22;
            Q22=makeQuery(id+"F7.opPattern","COPY",EDGE,{"derivedFrom":makeQuery(id+"F5.opPattern","COPY",EDGE,{"derivedFrom":makeQuery(id+"F3.opExtrude","CAP_EDGE",EDGE,{"disambiguationData":[OSD([sQuery(id+"F2.wireOp",EDGE,"E46")])],"isStart":false}),"instanceName":"1"}),"instanceName":"1"});
            fillet(context, id + "F10", {"entities" : qUnion([Q0, Q1, Q2, Q3, Q4, Q5, Q6, Q7, Q8, Q9, Q10, Q11, Q12, Q13, Q14, Q15, Q16, Q17, Q18, Q19, Q20, Q21, Q22]), "radius" : 1 * mm, "tangentPropagation" : true, "allowEdgeOverflow" : false});
        }
    });
